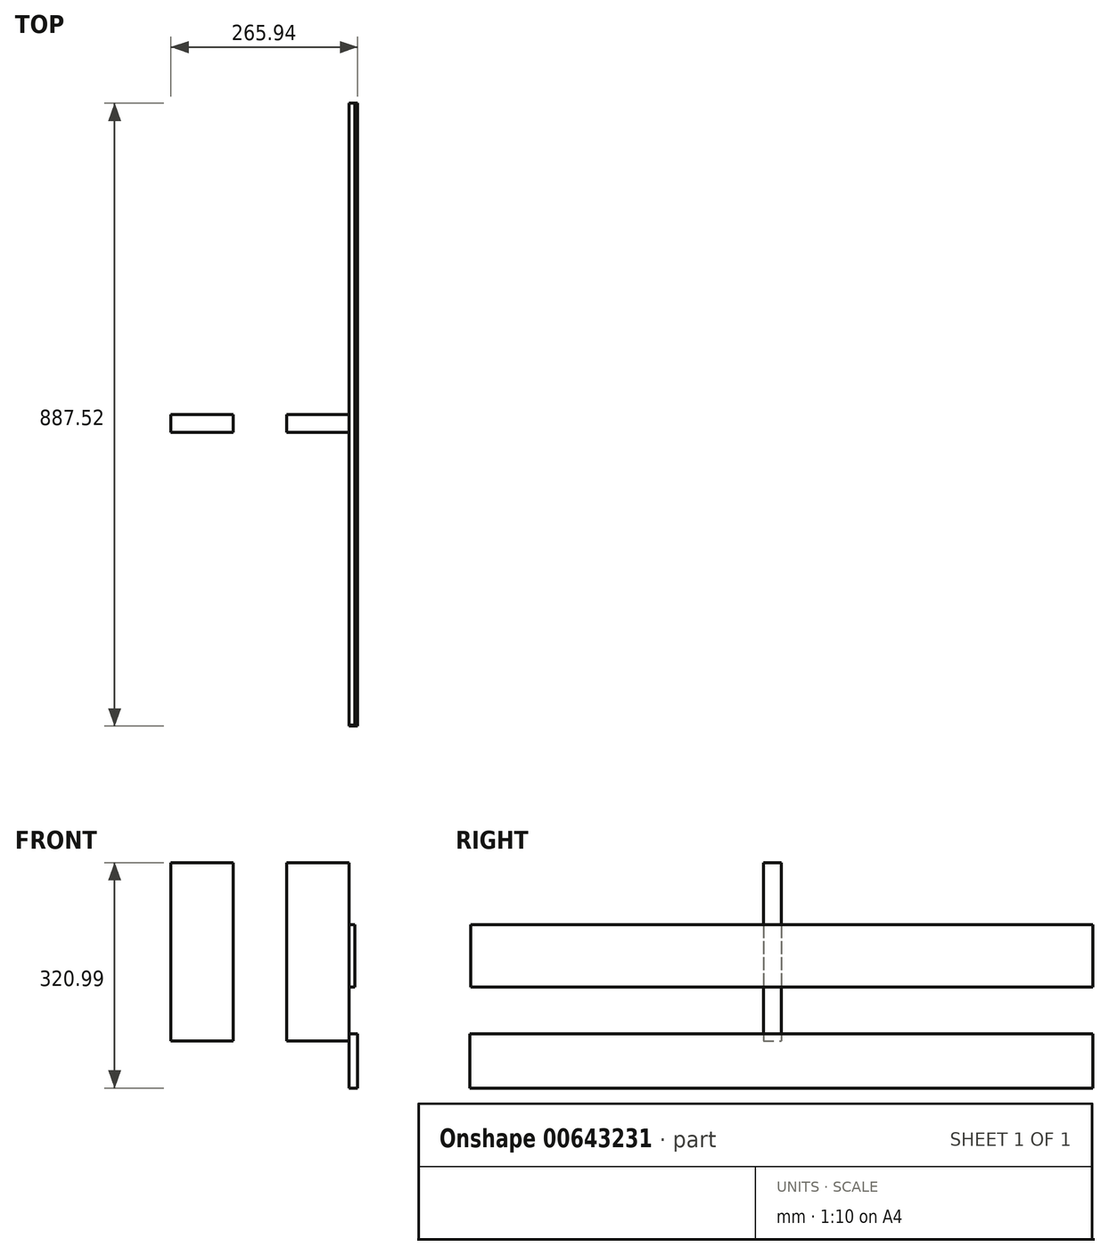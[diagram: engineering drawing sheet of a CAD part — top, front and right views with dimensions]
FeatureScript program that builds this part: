
annotation { "Feature Type Name" : "Feature", "Feature Type Description" : "" }
export const myFeature = defineFeature(function(context is Context, id is Id, definition is map)
    precondition{}
    {
        {
            var Q0;
            Q0=qCreatedBy(makeId("Front.planeOp"),FACE);
            var sketch = newSketch(context, id + "F0", { "sketchPlane" : qUnion([Q0])});
            skLineSegment(sketch, "E0.bottom", {"start": v(-88.9, 150.92) * mm, "end": v(0, 150.92) * mm});
            skLineSegment(sketch, "E0.top", {"start": v(-88.9, -103.08) * mm, "end": v(0, -103.08) * mm});
            skLineSegment(sketch, "E0.left", {"start": v(-88.9, 150.92) * mm, "end": v(-88.9, -103.08) * mm});
            skLineSegment(sketch, "E0.right", {"start": v(0, 150.92) * mm, "end": v(0, -103.08) * mm});
            skLineSegment(sketch, "E1", {"start": v(-88.9, 150.92) * mm, "end": v(-165.1, 150.92) * mm, "construction": true});
            skLineSegment(sketch, "E2", {"start": v(-165.1, 150.92) * mm, "end": v(-165.1, -103.08) * mm});
            skLineSegment(sketch, "E3", {"start": v(-165.1, -103.08) * mm, "end": v(-254, -103.08) * mm});
            skLineSegment(sketch, "E4", {"start": v(-254, -103.08) * mm, "end": v(-254, 150.92) * mm});
            skLineSegment(sketch, "E5", {"start": v(-254, 150.92) * mm, "end": v(-165.1, 150.92) * mm});
            skSolve(sketch);
        }
        {
            var Q0;
            Q0=qCreatedBy(makeId("Right.planeOp"),FACE);
            var sketch = newSketch(context, id + "F1", { "sketchPlane" : qUnion([Q0])});
            skLineSegment(sketch, "E6.bottom", {"start": v(-442.15, 62.55) * mm, "end": v(443.9, 62.55) * mm});
            skLineSegment(sketch, "E6.top", {"start": v(-442.15, -26.35) * mm, "end": v(443.9, -26.35) * mm});
            skLineSegment(sketch, "E6.left", {"start": v(-442.15, 62.55) * mm, "end": v(-442.15, -26.35) * mm});
            skLineSegment(sketch, "E6.right", {"start": v(443.9, 62.55) * mm, "end": v(443.9, -26.35) * mm});
            skLineSegment(sketch, "E7.bottom", {"start": v(-443.63, -93.03) * mm, "end": v(443.9, -93.03) * mm});
            skLineSegment(sketch, "E7.top", {"start": v(-443.63, -170.07) * mm, "end": v(443.9, -170.07) * mm});
            skLineSegment(sketch, "E7.left", {"start": v(-443.63, -93.03) * mm, "end": v(-443.63, -170.07) * mm});
            skLineSegment(sketch, "E7.right", {"start": v(443.9, -93.03) * mm, "end": v(443.9, -170.07) * mm});
            skSolve(sketch);
        }
        {
            var Q0;
            Q0=makeQuery(id+"F1.imprint","IMPRINT",FACE,{"disambiguationData":[TD([[makeQuery(id+"F1.imprint","IMPRINT",EDGE,{"derivedFrom":sQuery(id+"F1.wireOp",EDGE,"E6.bottom")}),-1.0]])]});
            var sketch = newSketch(context, id + "F2", { "sketchPlane" : qUnion([Q0])});
            skSolve(sketch);
        }
        {
            var Q0;
            Q0=makeQuery(id+"F1.imprint","IMPRINT",FACE,{"disambiguationData":[TD([[makeQuery(id+"F1.imprint","IMPRINT",EDGE,{"derivedFrom":sQuery(id+"F1.wireOp",EDGE,"E7.bottom")}),-1.0]])]});
            var Q1;
            Q1=makeQuery(id+"F1.imprint","IMPRINT",FACE,{"disambiguationData":[TD([[makeQuery(id+"F1.imprint","IMPRINT",EDGE,{"derivedFrom":sQuery(id+"F1.wireOp",EDGE,"E6.bottom")}),-1.0]])]});
            extrude(context, id + "F3", {"entities" : qUnion([Q0, Q1]), "depth" : 8.13 * mm, "offsetDistance" : 25.4 * mm});
        }
        {
            var Q0;
            Q0=makeQuery(id+"F3.opExtrude","CAP_FACE",FACE,{"disambiguationData":[OSD([sQuery(id+"F1.wireOp",EDGE,"E7.bottom"),sQuery(id+"F1.wireOp",EDGE,"E7.top"),sQuery(id+"F1.wireOp",EDGE,"E7.left"),sQuery(id+"F1.wireOp",EDGE,"E7.right")])],"isStart":false});
            extrude(context, id + "F4", {"entities" : qUnion([Q0]), "operationType" : NewBodyOperationType.ADD, "depth" : 3.8 * mm, "offsetDistance" : 25.4 * mm});
        }
        {
            var Q0;
            Q0=makeQuery(id+"F0.imprint","IMPRINT",FACE,{"disambiguationData":[TD([[makeQuery(id+"F0.imprint","IMPRINT",EDGE,{"derivedFrom":sQuery(id+"F0.wireOp",EDGE,"E0.bottom")}),-1.0]])]});
            var sketch = newSketch(context, id + "F5", { "sketchPlane" : qUnion([Q0])});
            skSolve(sketch);
        }
        {
            var Q0;
            Q0=makeQuery(id+"F5.imprint","IMPRINT",FACE,{"disambiguationData":[TD([[makeQuery(id+"F5.imprint","IMPRINT",EDGE,{"derivedFrom":makeQuery(id+"F0.imprint","IMPRINT",EDGE,{"derivedFrom":sQuery(id+"F0.wireOp",EDGE,"E0.bottom")})}),-1.0]])]});
            var sketch = newSketch(context, id + "F6", { "sketchPlane" : qUnion([Q0])});
            skSolve(sketch);
        }
        {
            var Q0;
            Q0=makeQuery(id+"F2.imprint","IMPRINT",FACE,{"disambiguationData":[TD([[makeQuery(id+"F2.imprint","IMPRINT",EDGE,{"derivedFrom":makeQuery(id+"F1.imprint","IMPRINT",EDGE,{"derivedFrom":sQuery(id+"F1.wireOp",EDGE,"E6.bottom")})}),-1.0]])]});
            var sketch = newSketch(context, id + "F7", { "sketchPlane" : qUnion([Q0])});
            skSolve(sketch);
        }
        {
            var Q0;
            Q0=makeQuery(id+"F6.imprint","IMPRINT",FACE,{"disambiguationData":[TD([[makeQuery(id+"F6.imprint","IMPRINT",EDGE,{"derivedFrom":makeQuery(id+"F5.imprint","IMPRINT",EDGE,{"derivedFrom":makeQuery(id+"F0.imprint","IMPRINT",EDGE,{"derivedFrom":sQuery(id+"F0.wireOp",EDGE,"E0.bottom")})})}),-1.0]])]});
            var Q1;
            Q1=makeQuery(id+"F0.imprint","IMPRINT",FACE,{"disambiguationData":[TD([[makeQuery(id+"F0.imprint","IMPRINT",EDGE,{"derivedFrom":sQuery(id+"F0.wireOp",EDGE,"E2")}),-1.0]])]});
            extrude(context, id + "F8", {"entities" : qUnion([Q0, Q1]), "depth" : 25.4 * mm, "offsetDistance" : 25.4 * mm});
        }
    });
